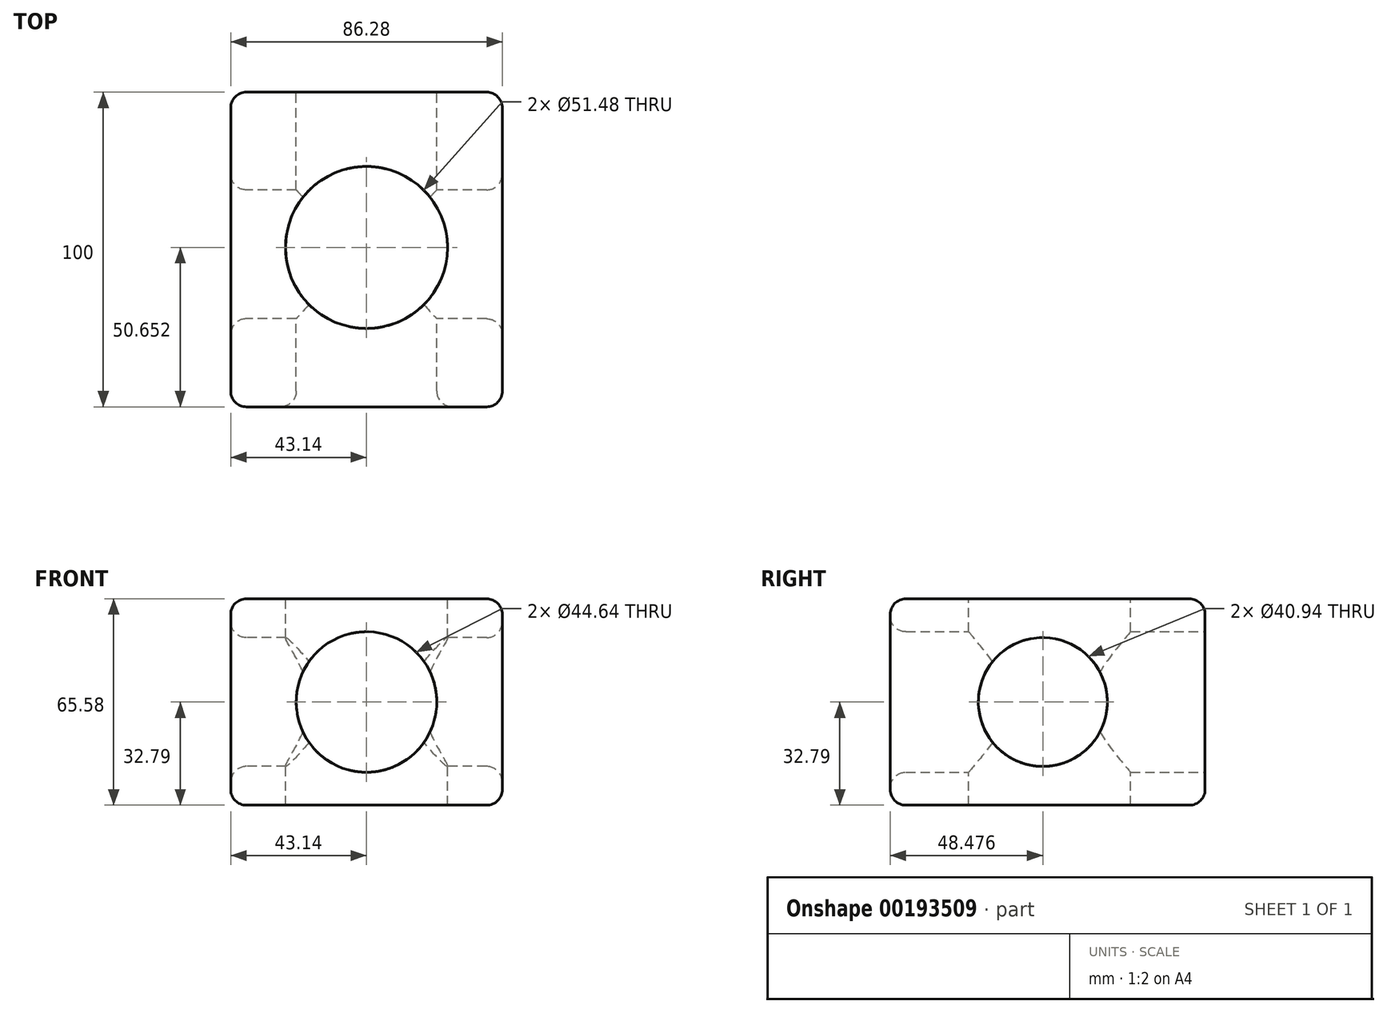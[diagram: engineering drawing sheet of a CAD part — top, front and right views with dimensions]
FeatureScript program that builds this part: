
annotation { "Feature Type Name" : "Feature", "Feature Type Description" : "" }
export const myFeature = defineFeature(function(context is Context, id is Id, definition is map)
    precondition{}
    {
        {
            var Q0;
            Q0=qCreatedBy(makeId("Front.planeOp"),FACE);
            var sketch = newSketch(context, id + "F0", { "sketchPlane" : qUnion([Q0])});
            skLineSegment(sketch, "E0.bottom", {"start": v(43.14, 32.8) * mm, "end": v(-43.14, 32.8) * mm});
            skLineSegment(sketch, "E0.top", {"start": v(43.14, -32.8) * mm, "end": v(-43.14, -32.8) * mm});
            skLineSegment(sketch, "E0.left", {"start": v(43.14, 32.8) * mm, "end": v(43.14, -32.8) * mm});
            skLineSegment(sketch, "E0.right", {"start": v(-43.14, 32.8) * mm, "end": v(-43.14, -32.8) * mm});
            skPoint(sketch, "E0.middle", {"position": v(0, 0) * mm});
            skSolve(sketch);
        }
        {
            var Q0;
            Q0=makeQuery(id+"F0.imprint","IMPRINT",FACE,{"disambiguationData":[TD([[makeQuery(id+"F0.imprint","IMPRINT",EDGE,{"derivedFrom":sQuery(id+"F0.wireOp",EDGE,"E0.bottom")}),1.0]])]});
            extrude(context, id + "F1", {"entities" : qUnion([Q0]), "depth" : 100 * mm});
        }
        {
            var Q0;
            Q0=makeQuery(id+"F1.opExtrude","CAP_FACE",FACE,{"disambiguationData":[OSD([sQuery(id+"F0.wireOp",EDGE,"E0.bottom"),sQuery(id+"F0.wireOp",EDGE,"E0.top"),sQuery(id+"F0.wireOp",EDGE,"E0.left"),sQuery(id+"F0.wireOp",EDGE,"E0.right")])],"isStart":true});
            var sketch = newSketch(context, id + "F2", { "sketchPlane" : qUnion([Q0])});
            skCircle(sketch, "E1", {"center": v(0, 0) * mm, "radius": 22.32 * mm});
            skSolve(sketch);
        }
        {
            var Q0;
            Q0 = qSketchRegion(id + "F2", true);
            extrude(context, id + "F3", {"entities" : qUnion([Q0]), "operationType" : NewBodyOperationType.REMOVE, "oppositeDirection" : true, "depth" : 115.4 * mm});
        }
        {
            var Q0;
            Q0=makeQuery(id+"F1.opExtrude","SWEPT_FACE",FACE,{"disambiguationData":[OSD([sQuery(id+"F0.wireOp",EDGE,"E0.right")])]});
            var sketch = newSketch(context, id + "F4", { "sketchPlane" : qUnion([Q0])});
            skCircle(sketch, "E2", {"center": v(51.52, 0) * mm, "radius": 20.47 * mm});
            skSolve(sketch);
        }
        {
            var Q0;
            Q0 = qSketchRegion(id + "F4", true);
            extrude(context, id + "F5", {"entities" : qUnion([Q0]), "operationType" : NewBodyOperationType.REMOVE, "oppositeDirection" : true, "depth" : 100.4 * mm});
        }
        {
            var Q0;
            Q0=makeQuery(id+"F1.opExtrude","SWEPT_FACE",FACE,{"disambiguationData":[OSD([sQuery(id+"F0.wireOp",EDGE,"E0.bottom")])]});
            var sketch = newSketch(context, id + "F6", { "sketchPlane" : qUnion([Q0])});
            skCircle(sketch, "E3", {"center": v(0, -49.35) * mm, "radius": 25.74 * mm});
            skSolve(sketch);
        }
        {
            var Q0;
            Q0 = qSketchRegion(id + "F6", true);
            extrude(context, id + "F7", {"entities" : qUnion([Q0]), "operationType" : NewBodyOperationType.REMOVE, "oppositeDirection" : true, "depth" : 93 * mm});
        }
        {
            var Q0;
            Q0=makeQuery(id+"F1.opExtrude","CAP_EDGE",EDGE,{"disambiguationData":[OSD([sQuery(id+"F0.wireOp",EDGE,"E0.bottom")])],"isStart":true});
            var Q1;
            Q1=makeQuery(id+"F1.opExtrude","CAP_EDGE",EDGE,{"disambiguationData":[OSD([sQuery(id+"F0.wireOp",EDGE,"E0.top")])],"isStart":true});
            fillet(context, id + "F8", {"entities" : qUnion([Q0, Q1]), "radius" : 5 * mm, "tangentPropagation" : true, "allowEdgeOverflow" : false});
        }
        {
            var Q0;
            Q0=makeQuery(id+"F1.opExtrude","CAP_FACE",FACE,{"disambiguationData":[OSD([sQuery(id+"F0.wireOp",EDGE,"E0.bottom"),sQuery(id+"F0.wireOp",EDGE,"E0.top"),sQuery(id+"F0.wireOp",EDGE,"E0.left"),sQuery(id+"F0.wireOp",EDGE,"E0.right")])],"isStart":false});
            var Q1;
            Q1=makeQuery(id+"F1.opExtrude","CAP_EDGE",EDGE,{"disambiguationData":[OSD([sQuery(id+"F0.wireOp",EDGE,"E0.left")])],"isStart":false});
            var Q2;
            Q2=makeQuery(id+"F1.opExtrude","CAP_EDGE",EDGE,{"disambiguationData":[OSD([sQuery(id+"F0.wireOp",EDGE,"E0.right")])],"isStart":false});
            var Q3;
            Q3=makeQuery(id+"F1.opExtrude","SWEPT_FACE",FACE,{"disambiguationData":[OSD([sQuery(id+"F0.wireOp",EDGE,"E0.right")])]});
            var Q4;
            Q4=makeQuery(id+"F1.opExtrude","SWEPT_FACE",FACE,{"disambiguationData":[OSD([sQuery(id+"F0.wireOp",EDGE,"E0.left")])]});
            fillet(context, id + "F9", {"entities" : qUnion([Q0, Q1, Q2, Q3, Q4]), "radius" : 5 * mm, "tangentPropagation" : true, "allowEdgeOverflow" : false});
        }
    });
